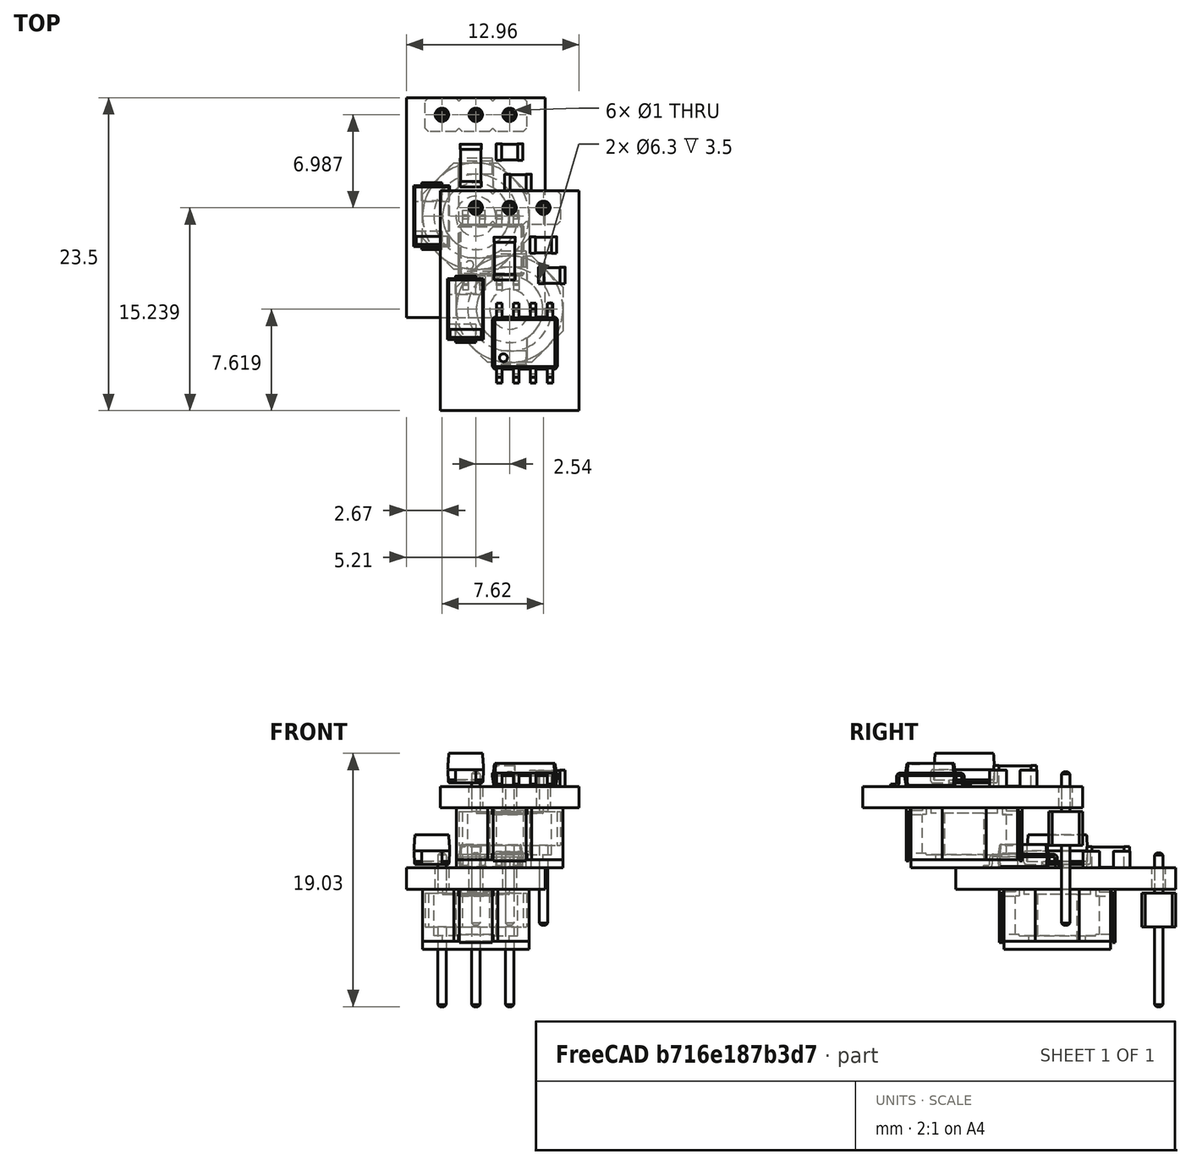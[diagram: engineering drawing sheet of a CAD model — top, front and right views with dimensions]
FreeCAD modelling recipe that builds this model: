
FCSTD DOCUMENT  (FreeCAD 0.17R13528 (Git))
Label: OKI_78SR_horizontal
License: All rights reserved
LicenseURL: http://en.wikipedia.org/wiki/All_rights_reserved
objects: Part::Feature×9, App::Part×5, Part::MultiFuse×2, Sketcher::SketchObject×1
note: 12 computed .brp shape members not serialized (recipe doc carries the construction recipe); baked Part::Feature solids carry a one-line shape summary decoded from their .brp

FEATURE [Part::Feature] Pcb
  Placement = pos=(-78.74,83.185,0) rot=(0,0,1;0rad)
  shape: bbox 10.41 x 16.51 x 1.6 mm, 10 faces (baked)
FEATURE [Sketcher::SketchObject] PCB_Sketch
  sketch-geometry (5):
    g0: LineSegment StartX=5.207 StartY=-8.255 StartZ=0 EndX=5.207 EndY=8.255 EndZ=0
    g1: LineSegment StartX=-5.207 StartY=-8.255 StartZ=0 EndX=5.207 EndY=-8.255 EndZ=0
    g2: LineSegment StartX=-5.207 StartY=8.255 StartZ=0 EndX=-5.207 EndY=-8.255 EndZ=0
    g3: LineSegment StartX=0 StartY=8.255 StartZ=0 EndX=5.207 EndY=8.255 EndZ=0
    g4: LineSegment StartX=0 StartY=8.255 StartZ=0 EndX=-5.207 EndY=8.255 EndZ=0
  constraints (5):
    c: Vertical(g0)
    c: Horizontal(g1)
    c: Vertical(g2)
    c: Horizontal(g3)
    c: Horizontal(g4)
FEATURE [App::Part] Board_Geoms
  Group = -> [Pcb,PCB_Sketch]
  Origin = -> Origin
FEATURE [Part::Feature] Shape  label="C_0805_2012Metric_"
  Placement = pos=(2.54,4.191,0) rot=(0,0,1;0rad)
  shape: bbox 2 x 1.25 x 1.25 mm, 28 faces (baked)
FEATURE [Part::Feature] Shape001  label="C_0805_2012Metric_001"
  Placement = pos=(3.175,1.905,0) rot=(0,0,1;0rad)
  shape: bbox 2 x 1.25 x 1.25 mm, 28 faces (baked)
FEATURE [Part::Feature] Shape002  label="PinHeader_1x03_P254mm_Vertical_"
  Placement = pos=(-2.54,6.985,-1.88) rot=(0.707107,-0.707107,0;3.14159rad)
  shape: bbox 7.62 x 2.54 x 11.54 mm, 76 faces (baked)
FEATURE [Part::Feature] Shape003  label="SOIC_8_39x49mm_P127mm_"
  Placement = pos=(1.143,-3.175,0) rot=(0,0,1;1.5708rad)
  shape: bbox 4.9 x 6 x 1.75 mm, 156 faces (baked)
FEATURE [Part::Feature] Shape004  label="D_SMA_"
  Placement = pos=(-3.302,-0.635,0.28) rot=(0,0,1;1.5708rad)
  shape: bbox 2.7 x 5 x 2.22 mm, 41 faces (baked)
FEATURE [Part::Feature] Shape005  label="C_1206_3216Metric_"
  Placement = pos=(-0.381,3.175,0) rot=(0,0,1;1.5708rad)
  shape: bbox 1.6 x 3.2 x 1.6 mm, 28 faces (baked)
FEATURE [App::Part] Top
  Group = -> [Shape,Shape001,Shape003,Shape004,Shape005]
  License = CC BY 3.0
  LicenseURL = http://creativecommons.org/licenses/by/3.0/
  Origin = -> Origin003
FEATURE [Part::Feature] Shape006  label="L_CDRH8D43_8x8mm_H4.5_"
  Placement = pos=(0,-0.635,-1.6) rot=(0.707107,0.707107,0;3.14159rad)
  shape: bbox 8 x 8.7 x 4.5 mm, 58 faces, 3 solids (baked)
FEATURE [App::Part] Bot
  Group = -> [Shape002,Shape006]
  License = CC BY 3.0
  LicenseURL = http://creativecommons.org/licenses/by/3.0/
  Origin = -> Origin004
FEATURE [App::Part] Step_Models
  Group = -> [Top,Bot]
  Origin = -> Origin002
FEATURE [App::Part] Board  label="OKI-78SR_horizontal"
  Group = -> [Board_Geoms,Step_Models]
  Origin = -> Origin001
FEATURE [Part::MultiFuse] L_CDRH8D43_8x8mm_H4_5__mp_cp  label="L_CDRH8D43_8x8mm_H4.5__fd"
  Refine = true
  Shapes = -> [Shape006,Shape002,Shape005,Shape004,Shape003,Shape001,Shape,Pcb]
FEATURE [Part::MultiFuse] L_CDRH8D43_8x8mm_H4_5__mp_cp001  label="L_CDRH8D43_8x8mm_H4.5__fd001"
  Refine = true
  Shapes = -> [Shape006,Pcb,Shape,Shape001,Shape002,Shape003,Shape004,Shape005]
FEATURE [Part::Feature] Shape020  label="Converter_DCDC_muRata_OKI-78SR_horizontal"
  shape: bbox 10.41 x 16.51 x 12.92 mm, 406 faces, 4 solids (baked)
